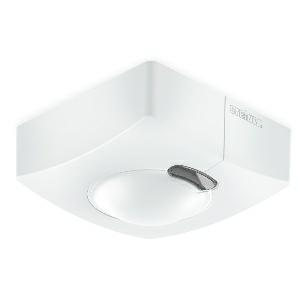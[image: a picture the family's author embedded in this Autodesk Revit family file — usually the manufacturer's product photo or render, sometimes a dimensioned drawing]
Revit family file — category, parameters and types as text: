
# Revit family: hf_3360_058210
name_source: partatom
category: Elektroinstallationen
revit_build: Autodesk Revit 2016 (Build: 20190508_0715(x64)
units: mm (PartAtom-declared; Revit-internal decimal feet)

## family parameters
Basisbauteil = Fläche
Beim Laden mit Abzugskörper schneiden = Nein
Bemaßung runder Anschluss = Durchmesser verwenden
Beschriftungsausrichtung beibehalten = Nein
Gemeinsam genutzt = Nein
Raumberechnungspunkt = Nein
Teiletyp = Normal

## types (1)
- HF 3360
    Apparent Load = 0 VA
    Beschreibung = Type: Motion detectors; Dimensions (L x W x H): 52 x 95 x 95 mm; Sensor Technology: High frequency; Application, place: Indoors; Application, room: function room / ancillary room, stairwell, WC / washroom, multi-storey / underground car park, Indoors; Installation site: wall, ceiling, corner; Installation: Surface wiring; HF-system: 5,8 GHz; Mounting height: 2,00 – 4,00 m; Optimum mounting height: 2,8 m; Detection angle: 360 °; Sneak-by guard: Yes; Twilight setting TEACH: Yes; Time setting: 0 sec – 1092 min; Basic light level function: Yes; KNX functions: Photo-cell controller, Basic light level function, Light level, HVAC output, Constant-lighting control, Light output 2x, Presence output, Day / night function; With bus coupling: Yes; Settings via: ETS software, Remote control, Bus, Smart Remote; IP-rating: IP54; Material: Plastic; Colour: white; Colour, RAL: 9003; Version: KNX - surface, sq.; PU1, EAN: 4007841058210
    Height = 95 mm
    Hersteller = Steinel
    Length = 52 mm  [stored 0.170604 ft]
    ModVariant = Nein
    Modell = 058210
    Mounting Type = Surface mounted
    Number of Poles = 1
    OnlyDefault = Ja
    Power Factor = 1
    Product Name = HF 3360
    Product group = Sensor-switched indoor light
    ProductGroupID = 30
    Protection Class = Protection class
    Protection Degree = IP 54
    RlxData = <blob elided: 25037 chars, md5=3674230e>
    SensorDataFile = {"IESDataFiles":[]}
    Typenbild = produkt1_058210.jpg
    Typenkommentare = Product without accessories
    URL = http://relux.com
    VarID = ---
    Voltage = 0 V
    Vorgabe-Ansicht = 1800 mm
    Weight = 0.00 kg
    Width = 95 mm

note: [stored X ft] marks values corroborated as IEEE doubles in the binary element streams (Revit-internal decimal feet)

## geometry (parser evidence)
native form markers: Blend x4, Sweep x12
no freeform markers — native parametric forms only
